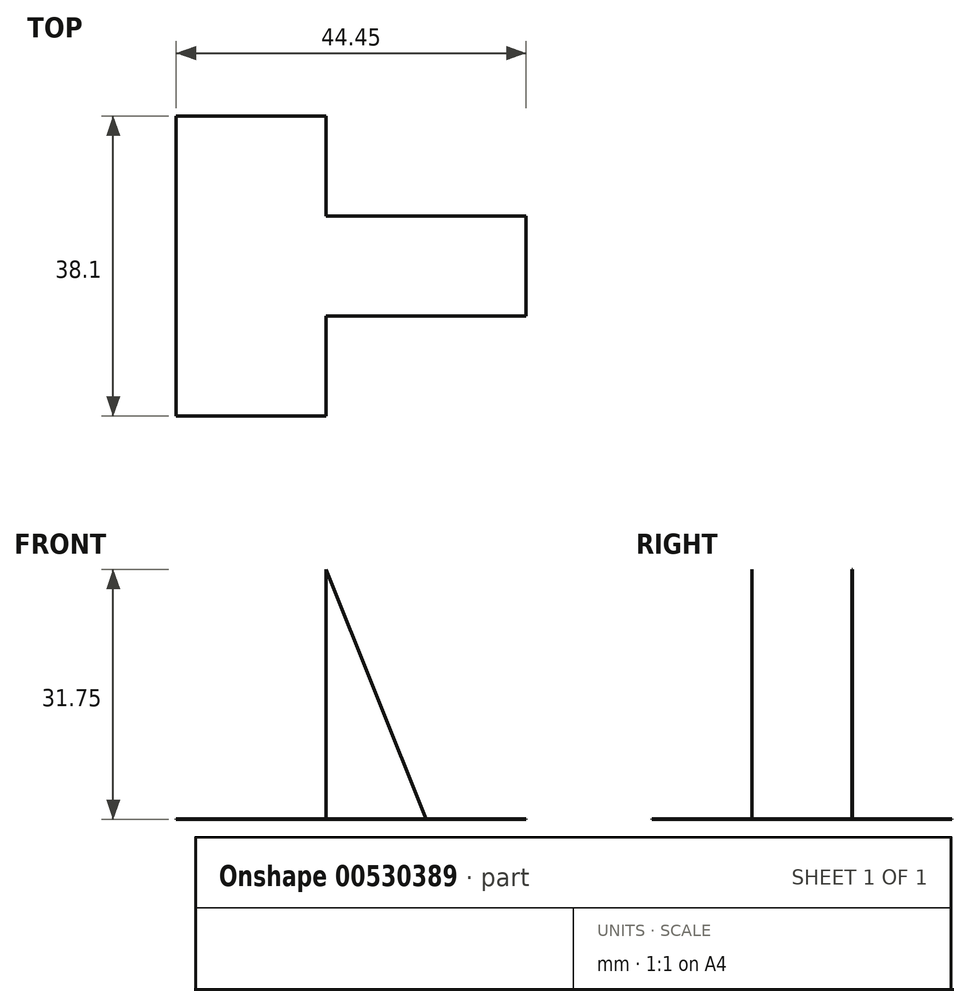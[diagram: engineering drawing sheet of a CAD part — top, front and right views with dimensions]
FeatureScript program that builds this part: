
annotation { "Feature Type Name" : "Feature", "Feature Type Description" : "" }
export const myFeature = defineFeature(function(context is Context, id is Id, definition is map)
    precondition{}
    {
        {
            var Q0;
            Q0=qCreatedBy(makeId("Top.planeOp"),FACE);
            var sketch = newSketch(context, id + "F0", { "sketchPlane" : qUnion([Q0])});
            skLineSegment(sketch, "E0", {"start": v(-44.45, 38.1) * mm, "end": v(-44.45, 0) * mm});
            skLineSegment(sketch, "E1", {"start": v(-44.45, 0) * mm, "end": v(-25.4, 0) * mm});
            skLineSegment(sketch, "E2", {"start": v(-25.4, 0) * mm, "end": v(-25.4, 12.7) * mm});
            skLineSegment(sketch, "E3", {"start": v(-25.4, 12.7) * mm, "end": v(0, 12.7) * mm});
            skLineSegment(sketch, "E4", {"start": v(-44.45, 38.1) * mm, "end": v(-25.4, 38.1) * mm});
            skLineSegment(sketch, "E5", {"start": v(-25.4, 38.1) * mm, "end": v(-25.4, 25.4) * mm});
            skLineSegment(sketch, "E6", {"start": v(-25.4, 25.4) * mm, "end": v(0, 25.4) * mm});
            skLineSegment(sketch, "E7", {"start": v(0, 25.4) * mm, "end": v(0, 12.7) * mm});
            skSolve(sketch);
        }
        {
            var Q0;
            Q0=makeQuery(id+"F0.imprint","IMPRINT",FACE,{"disambiguationData":[TD([[makeQuery(id+"F0.imprint","IMPRINT",EDGE,{"derivedFrom":sQuery(id+"F0.wireOp",EDGE,"E0")}),1.0]])]});
            extrude(context, id + "F1", {"entities" : qUnion([Q0]), "depth" : 5 / 101.6 * mm, "offsetDistance" : 25.4 * mm});
        }
        {
            var Q0;
            Q0=makeQuery(id+"F1.opExtrude","SWEPT_FACE",FACE,{"disambiguationData":[OSD([sQuery(id+"F0.wireOp",EDGE,"E3")])]});
            var sketch = newSketch(context, id + "F2", { "sketchPlane" : qUnion([Q0])});
            skLineSegment(sketch, "E8", {"start": v(-12.7, 31.75) * mm, "end": v(0, 0) * mm});
            skLineSegment(sketch, "E9", {"start": v(0, 0) * mm, "end": v(0, 31.75) * mm});
            skLineSegment(sketch, "E10", {"start": v(0, 31.75) * mm, "end": v(-12.7, 31.75) * mm});
            skSolve(sketch);
        }
        {
            var Q0;
            Q0=makeQuery(id+"F2.imprint","IMPRINT",FACE,{"disambiguationData":[TD([[makeQuery(id+"F2.imprint","IMPRINT",EDGE,{"derivedFrom":sQuery(id+"F2.wireOp",EDGE,"E8")}),1.0]])]});
            extrude(context, id + "F3", {"entities" : qUnion([Q0]), "operationType" : NewBodyOperationType.REMOVE, "endBound" : BoundingType.THROUGH_ALL, "oppositeDirection" : true, "depth" : 25.4 * mm, "offsetDistance" : 25.4 * mm});
        }
        {
            var Q0;
            Q0=makeQuery(id+"F1.opExtrude","SWEPT_FACE",FACE,{"disambiguationData":[OSD([sQuery(id+"F0.wireOp",EDGE,"E3")])]});
            var sketch = newSketch(context, id + "F4", { "sketchPlane" : qUnion([Q0])});
            skLineSegment(sketch, "E11", {"start": v(-25.4, 31.75) * mm, "end": v(-12.7, 0) * mm});
            skLineSegment(sketch, "E12", {"start": v(-12.7, 0) * mm, "end": v(-25.4, 0) * mm});
            skLineSegment(sketch, "E13", {"start": v(-25.4, 31.75) * mm, "end": v(-25.4, 0) * mm});
            skLineSegment(sketch, "E14", {"start": v(-25.4, 0) * mm, "end": v(-44.45, 0) * mm});
            skSolve(sketch);
        }
        {
            var Q0;
            Q0=makeQuery(id+"F4.imprint","IMPRINT",FACE,{"disambiguationData":[TD([[makeQuery(id+"F4.imprint","IMPRINT",EDGE,{"derivedFrom":sQuery(id+"F4.wireOp",EDGE,"E11")}),-1.0]])]});
            extrude(context, id + "F5", {"entities" : qUnion([Q0]), "operationType" : NewBodyOperationType.ADD, "depth" : 2 / 101.6 * mm, "offsetDistance" : 25.4 * mm});
        }
        {
            var Q0;
            Q0=makeQuery(id+"F1.opExtrude","SWEPT_FACE",FACE,{"disambiguationData":[OSD([sQuery(id+"F0.wireOp",EDGE,"E6")])]});
            var sketch = newSketch(context, id + "F6", { "sketchPlane" : qUnion([Q0])});
            skLineSegment(sketch, "E15", {"start": v(25.4, 31.75) * mm, "end": v(12.7, 0) * mm});
            skLineSegment(sketch, "E16", {"start": v(25.4, 31.75) * mm, "end": v(25.4, 0) * mm});
            skLineSegment(sketch, "E17", {"start": v(25.4, 0) * mm, "end": v(12.7, 0) * mm});
            skSolve(sketch);
        }
        {
            var Q0;
            Q0=makeQuery(id+"F6.imprint","IMPRINT",FACE,{"disambiguationData":[TD([[makeQuery(id+"F6.imprint","IMPRINT",EDGE,{"derivedFrom":sQuery(id+"F6.wireOp",EDGE,"E15")}),1.0]])]});
            extrude(context, id + "F7", {"entities" : qUnion([Q0]), "operationType" : NewBodyOperationType.ADD, "depth" : 2 / 101.6 * mm, "offsetDistance" : 25.4 * mm});
        }
    });
